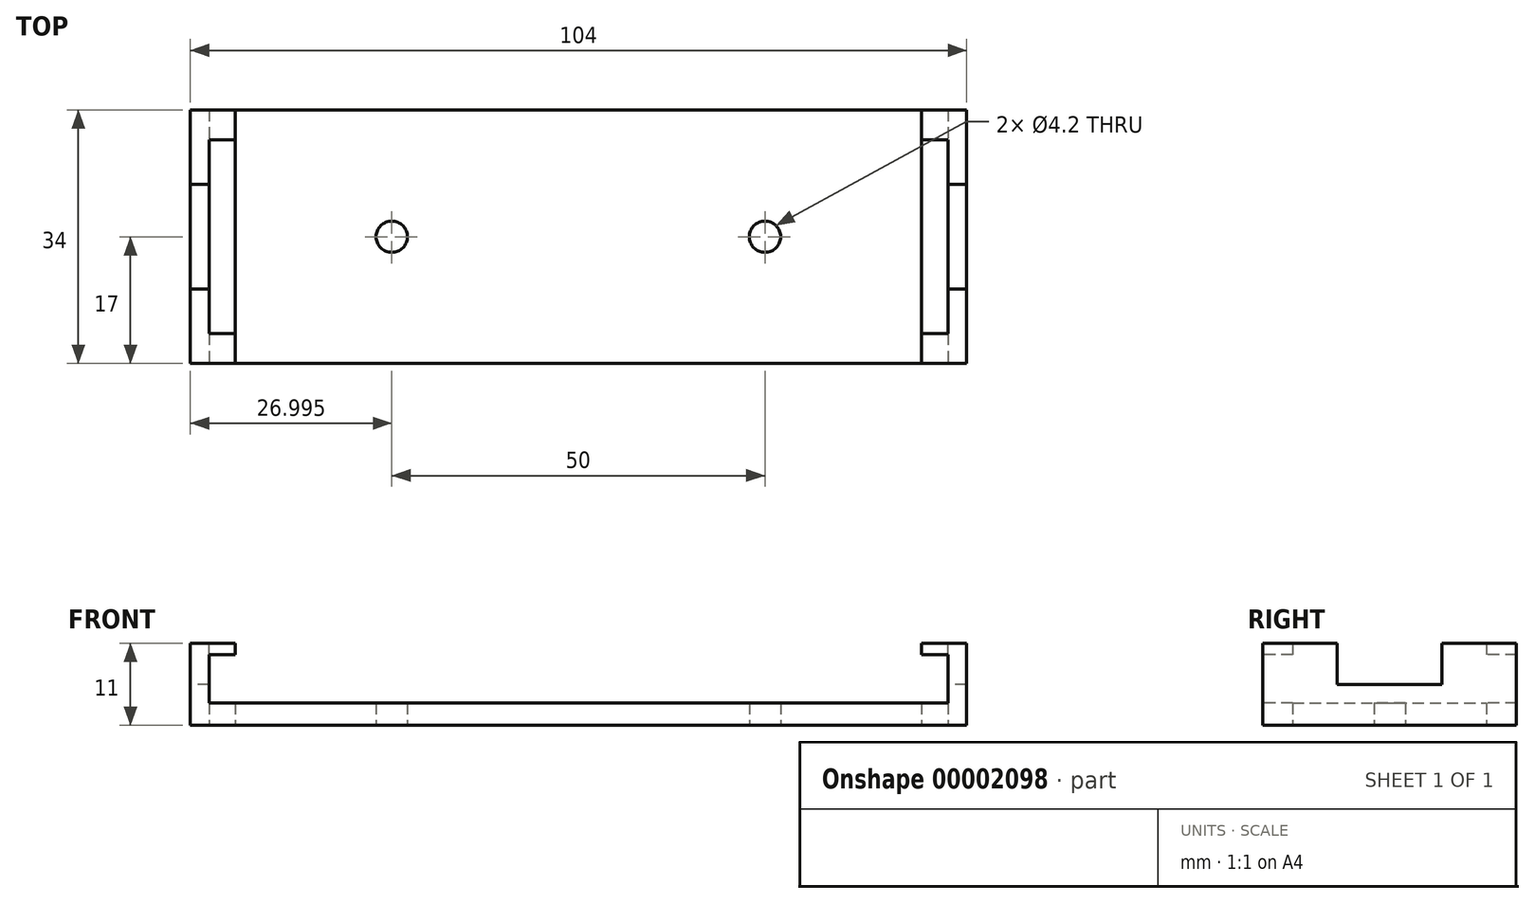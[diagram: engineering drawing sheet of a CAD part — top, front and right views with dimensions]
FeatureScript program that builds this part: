
annotation { "Feature Type Name" : "Feature", "Feature Type Description" : "" }
export const myFeature = defineFeature(function(context is Context, id is Id, definition is map)
    precondition{}
    {
        {
            var Q0;
            Q0=qCreatedBy(makeId("Top.planeOp"),FACE);
            var sketch = newSketch(context, id + "F0", { "sketchPlane" : qUnion([Q0])});
            skLineSegment(sketch, "E0.bottom", {"start": v(-48.18, 0) * mm, "end": v(55.82, 0) * mm});
            skLineSegment(sketch, "E0.top", {"start": v(-48.18, 34) * mm, "end": v(55.82, 34) * mm});
            skLineSegment(sketch, "E0.left", {"start": v(-48.18, 0) * mm, "end": v(-48.18, 34) * mm});
            skLineSegment(sketch, "E0.right", {"start": v(55.82, 0) * mm, "end": v(55.82, 34) * mm});
            skSolve(sketch);
        }
        {
            var Q0;
            Q0=makeQuery(id+"F0.imprint","IMPRINT",FACE,{"disambiguationData":[TD([[makeQuery(id+"F0.imprint","IMPRINT",EDGE,{"derivedFrom":sQuery(id+"F0.wireOp",EDGE,"E0.bottom")}),1.0]])]});
            extrude(context, id + "F1", {"entities" : qUnion([Q0]), "depth" : 3 * mm});
        }
        {
            var Q0;
            Q0=makeQuery(id+"F1.opExtrude","CAP_FACE",FACE,{"disambiguationData":[OSD([sQuery(id+"F0.wireOp",EDGE,"E0.bottom"),sQuery(id+"F0.wireOp",EDGE,"E0.top"),sQuery(id+"F0.wireOp",EDGE,"E0.left"),sQuery(id+"F0.wireOp",EDGE,"E0.right")])],"isStart":false});
            var sketch = newSketch(context, id + "F2", { "sketchPlane" : qUnion([Q0])});
            skLineSegment(sketch, "E1.bottom", {"start": v(-48.18, 34) * mm, "end": v(-42.18, 34) * mm});
            skLineSegment(sketch, "E1.top", {"start": v(-48.18, 0) * mm, "end": v(-42.18, 0) * mm});
            skLineSegment(sketch, "E1.left", {"start": v(-48.18, 34) * mm, "end": v(-48.18, 0) * mm});
            skLineSegment(sketch, "E1.right", {"start": v(-42.18, 34) * mm, "end": v(-42.18, 0) * mm});
            skLineSegment(sketch, "E2.bottom", {"start": v(-48.18, 0) * mm, "end": v(-44.18, 0) * mm});
            skLineSegment(sketch, "E3.bottom", {"start": v(55.82, 0) * mm, "end": v(51.82, 0) * mm});
            skLineSegment(sketch, "E3.left", {"start": v(55.82, 0) * mm, "end": v(55.82, 4) * mm});
            skLineSegment(sketch, "E4.bottom", {"start": v(55.82, 34) * mm, "end": v(49.82, 34) * mm});
            skLineSegment(sketch, "E4.top", {"start": v(55.82, 0) * mm, "end": v(49.82, 0) * mm});
            skLineSegment(sketch, "E4.left", {"start": v(55.82, 34) * mm, "end": v(55.82, 0) * mm});
            skLineSegment(sketch, "E4.right", {"start": v(49.82, 34) * mm, "end": v(49.82, 0) * mm});
            skSolve(sketch);
        }
        {
            var Q0;
            Q0 = qSketchRegion(id + "F2", true);
            extrude(context, id + "F3", {"entities" : qUnion([Q0]), "operationType" : NewBodyOperationType.ADD, "depth" : 8 * mm});
        }
        {
            var Q0;
            Q0=makeQuery(id+"F3.boolean.opBoolean","MERGE",FACE,{"derivedFrom":[makeQuery(id+"F1.opExtrude","SWEPT_FACE",FACE,{"disambiguationData":[OSD([sQuery(id+"F0.wireOp",EDGE,"E0.bottom")])]}),makeQuery(id+"F3.opExtrude","SWEPT_FACE",FACE,{"disambiguationData":[OSD([sQuery(id+"F2.wireOp",EDGE,"E2.bottom")])]}),makeQuery(id+"F3.opExtrude","SWEPT_FACE",FACE,{"disambiguationData":[OSD([sQuery(id+"F2.wireOp",EDGE,"E4.top")])]})]});
            var sketch = newSketch(context, id + "F4", { "sketchPlane" : qUnion([Q0])});
            skLineSegment(sketch, "E5.bottom", {"start": v(-42.18, 3) * mm, "end": v(-45.68, 3) * mm});
            skLineSegment(sketch, "E5.top", {"start": v(-42.18, 9.5) * mm, "end": v(-45.68, 9.5) * mm});
            skLineSegment(sketch, "E5.left", {"start": v(-42.18, 3) * mm, "end": v(-42.18, 9.5) * mm});
            skLineSegment(sketch, "E5.right", {"start": v(-45.68, 3) * mm, "end": v(-45.68, 9.5) * mm});
            skLineSegment(sketch, "E6.left", {"start": v(-42.18, 3) * mm, "end": v(-42.18, 9) * mm});
            skLineSegment(sketch, "E7.bottom", {"start": v(49.82, 3) * mm, "end": v(53.32, 3) * mm});
            skLineSegment(sketch, "E7.top", {"start": v(49.82, 9.5) * mm, "end": v(53.32, 9.5) * mm});
            skLineSegment(sketch, "E7.left", {"start": v(49.82, 3) * mm, "end": v(49.82, 9.5) * mm});
            skLineSegment(sketch, "E7.right", {"start": v(53.32, 3) * mm, "end": v(53.32, 9.5) * mm});
            skSolve(sketch);
        }
        {
            var Q0;
            Q0=makeQuery(id+"F4.imprint","IMPRINT",FACE,{"disambiguationData":[TD([[makeQuery(id+"F4.imprint","IMPRINT",EDGE,{"derivedFrom":sQuery(id+"F4.wireOp",EDGE,"E5.bottom")}),-1.0]])]});
            var Q1;
            Q1=makeQuery(id+"F4.imprint","IMPRINT",FACE,{"disambiguationData":[TD([[makeQuery(id+"F4.imprint","IMPRINT",EDGE,{"derivedFrom":sQuery(id+"F4.wireOp",EDGE,"E7.bottom")}),1.0]])]});
            extrude(context, id + "F5", {"entities" : qUnion([Q0, Q1]), "operationType" : NewBodyOperationType.REMOVE, "endBound" : BoundingType.THROUGH_ALL, "oppositeDirection" : true, "depth" : 34 * mm});
        }
        {
            var Q0;
            Q0=qCreatedBy(makeId("Top.planeOp"),FACE);
            var sketch = newSketch(context, id + "F6", { "sketchPlane" : qUnion([Q0])});
            skCircle(sketch, "E8", {"center": v(-21.18, 17) * mm, "radius": 2.1 * mm});
            skCircle(sketch, "E9", {"center": v(28.82, 17) * mm, "radius": 2.1 * mm});
            skSolve(sketch);
        }
        {
            var Q0;
            {Q0=qUnion([makeQuery(id+"F6.imprint","IMPRINT",FACE,{"disambiguationData":[TD([[makeQuery(id+"F6.imprint","IMPRINT",EDGE,{"derivedFrom":sQuery(id+"F6.wireOp",EDGE,"E8")}),1.0]])]}),makeQuery(id+"F6.imprint","IMPRINT",FACE,{"disambiguationData":[TD([[makeQuery(id+"F6.imprint","IMPRINT",EDGE,{"derivedFrom":sQuery(id+"F6.wireOp",EDGE,"E9")}),1.0]])]})]);}
            extrude(context, id + "F7", {"entities" : qUnion([Q0]), "operationType" : NewBodyOperationType.REMOVE, "depth" : 25.4 * mm});
        }
        {
            var Q0;
            Q0=qCreatedBy(makeId("Top.planeOp"),FACE);
            var sketch = newSketch(context, id + "F8", { "sketchPlane" : qUnion([Q0])});
            skLineSegment(sketch, "E10.bottom", {"start": v(-42.18, 30) * mm, "end": v(-45.68, 30) * mm});
            skLineSegment(sketch, "E10.top", {"start": v(-42.18, 4) * mm, "end": v(-45.68, 4) * mm});
            skLineSegment(sketch, "E10.left", {"start": v(-42.18, 30) * mm, "end": v(-42.18, 4) * mm});
            skLineSegment(sketch, "E10.right", {"start": v(-45.68, 30) * mm, "end": v(-45.68, 4) * mm});
            skLineSegment(sketch, "E11.bottom", {"start": v(49.82, 4) * mm, "end": v(53.32, 4) * mm});
            skLineSegment(sketch, "E11.top", {"start": v(49.82, 30) * mm, "end": v(53.32, 30) * mm});
            skLineSegment(sketch, "E11.left", {"start": v(49.82, 4) * mm, "end": v(49.82, 30) * mm});
            skLineSegment(sketch, "E11.right", {"start": v(53.32, 4) * mm, "end": v(53.32, 30) * mm});
            skSolve(sketch);
        }
        {
            var Q0;
            {Q0=qUnion([makeQuery(id+"F8.imprint","IMPRINT",FACE,{"disambiguationData":[TD([[makeQuery(id+"F8.imprint","IMPRINT",EDGE,{"derivedFrom":sQuery(id+"F8.wireOp",EDGE,"E10.bottom")}),1.0]])]}),makeQuery(id+"F8.imprint","IMPRINT",FACE,{"disambiguationData":[TD([[makeQuery(id+"F8.imprint","IMPRINT",EDGE,{"derivedFrom":sQuery(id+"F8.wireOp",EDGE,"E11.bottom")}),1.0]])]})]);}
            extrude(context, id + "F9", {"entities" : qUnion([Q0]), "operationType" : NewBodyOperationType.REMOVE, "depth" : 25 * mm});
        }
        {
            var Q0;
            Q0=makeQuery(id+"F3.boolean.opBoolean","MERGE",FACE,{"derivedFrom":[makeQuery(id+"F1.opExtrude","SWEPT_FACE",FACE,{"disambiguationData":[OSD([sQuery(id+"F0.wireOp",EDGE,"E0.left")])]}),makeQuery(id+"F3.opExtrude","SWEPT_FACE",FACE,{"disambiguationData":[OSD([sQuery(id+"F2.wireOp",EDGE,"E1.left")])]})]});
            var sketch = newSketch(context, id + "F10", { "sketchPlane" : qUnion([Q0])});
            skLineSegment(sketch, "E12.bottom", {"start": v(-24, 11) * mm, "end": v(-10, 11) * mm});
            skLineSegment(sketch, "E12.top", {"start": v(-24, 5.5) * mm, "end": v(-10, 5.5) * mm});
            skLineSegment(sketch, "E12.left", {"start": v(-24, 11) * mm, "end": v(-24, 5.5) * mm});
            skLineSegment(sketch, "E12.right", {"start": v(-10, 11) * mm, "end": v(-10, 5.5) * mm});
            skSolve(sketch);
        }
        {
            var Q0;
            Q0=makeQuery(id+"F10.imprint","IMPRINT",FACE,{"disambiguationData":[TD([[makeQuery(id+"F10.imprint","IMPRINT",EDGE,{"derivedFrom":sQuery(id+"F10.wireOp",EDGE,"E12.bottom")}),1.0]])]});
            extrude(context, id + "F11", {"entities" : qUnion([Q0]), "operationType" : NewBodyOperationType.REMOVE, "endBound" : BoundingType.THROUGH_ALL, "oppositeDirection" : true, "depth" : 25 * mm});
        }
    });
